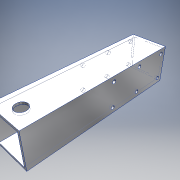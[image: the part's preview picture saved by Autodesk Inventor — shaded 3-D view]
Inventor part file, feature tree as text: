
AUTODESK INVENTOR PART (.ipt)
format: ipt  version: 2019 (Build 230136000, 136)  size: 143,872 bytes
history: native  units: in
note: dims shown in document units (in); Inventor stores cm internally (conversion verified against a paired STEP export)
features: extrude x3, sketch x3
ambient origin geometry x8: Origin, YZ Plane, XZ Plane, XY Plane, X Axis, Y Axis, Z Axis, Center Point
bodies: Solid1 (feature_tree)
feature tree (6):
  extrude  "Extrusion1"  Depth=0.125in
  extrude  "Extrusion2"  Depth=8.5in
  extrude  "Extrusion6"  Depth=3.5in
  sketch  "Sketch1"  dims[d0=2.0in d1=0.125in]
  sketch  "Sketch2"  dims[d2=8.5in d3=0.0in d4=0.21in]
  sketch  "Sketch4"  dims[d5=0.3in d6=3.5in d7=0.7in d8=18.0in d9=0.0in d13=0.625in d14=0.75in d17=0.19in d18=1.0in d21=1.0in d22=0.0in]
